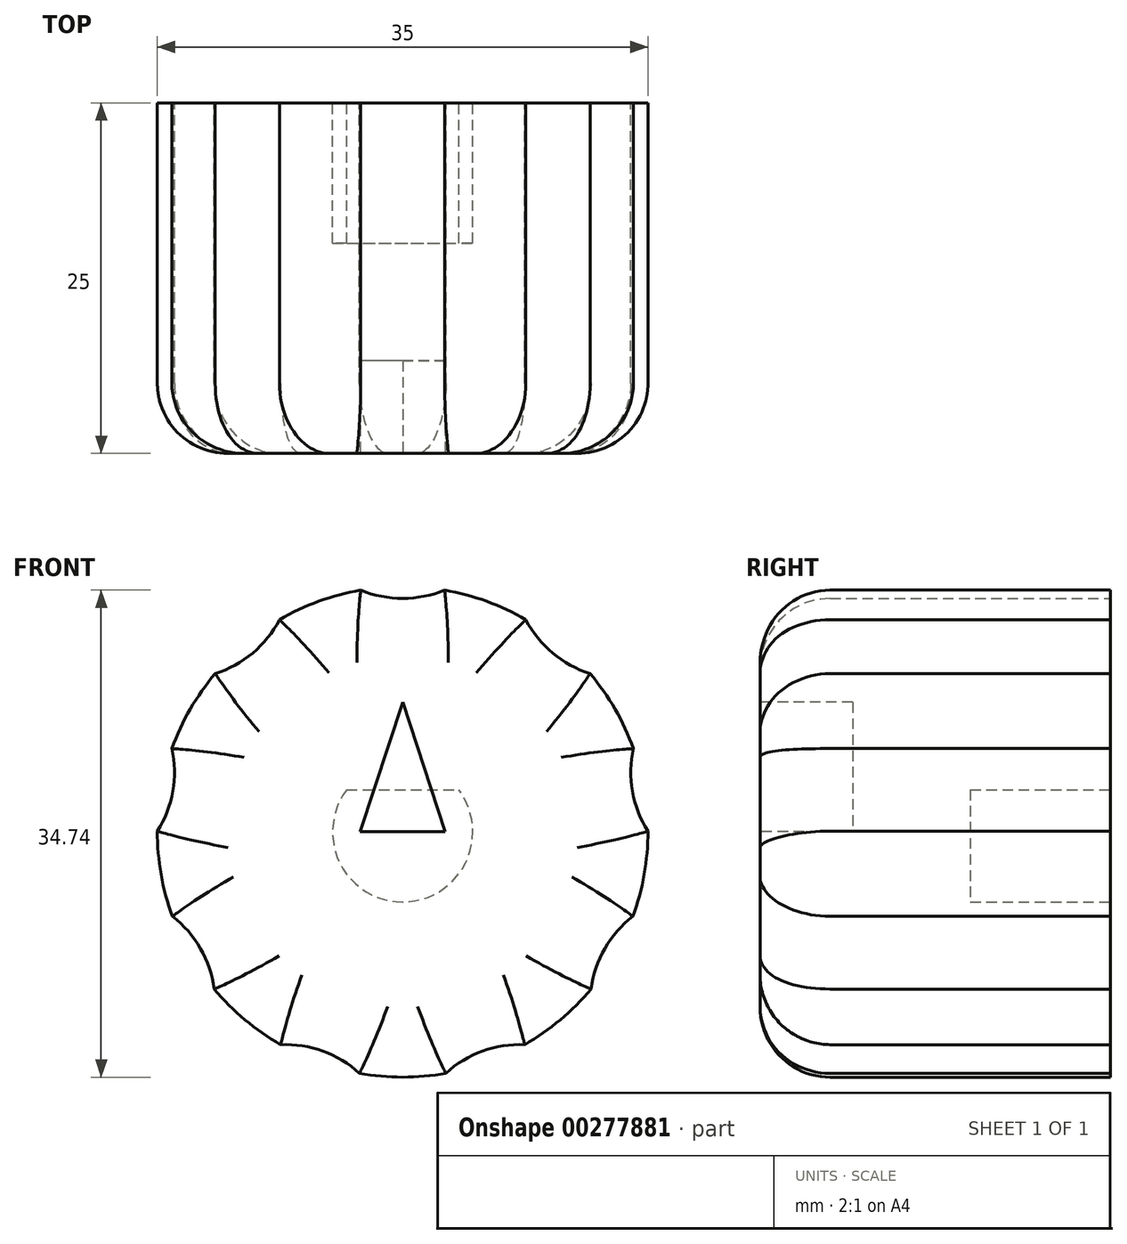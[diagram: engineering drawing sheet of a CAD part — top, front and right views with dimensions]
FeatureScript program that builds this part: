
annotation { "Feature Type Name" : "Feature", "Feature Type Description" : "" }
export const myFeature = defineFeature(function(context is Context, id is Id, definition is map)
    precondition{}
    {
        {
            var Q0;
            Q0=qCreatedBy(makeId("Front.planeOp"),FACE);
            var sketch = newSketch(context, id + "F0", { "sketchPlane" : qUnion([Q0])});
            skCircle(sketch, "E0", {"center": v(0, 0) * mm, "radius": 17.5 * mm});
            skCircle(sketch, "E1", {"center": v(0, 0) * mm, "radius": 5 * mm});
            skLineSegment(sketch, "E2", {"start": v(-4, 3) * mm, "end": v(4, 3) * mm});
            skLineSegment(sketch, "E3", {"start": v(-63, 45.04) * mm, "end": v(-24.6, 45.04) * mm, "construction": true});
            skLineSegment(sketch, "E4", {"start": v(-60.54, 31) * mm, "end": v(-26.33, 31.5) * mm, "construction": true});
            skLineSegment(sketch, "E5", {"start": v(-3, 17.24) * mm, "end": v(3, 17.24) * mm, "construction": true});
            skArc(sketch, "E6", {"start": v(-3, 17.24) * mm, "mid": v(0, 16.65) * mm, "end": v(3, 17.24) * mm});
            skArc(sketch, "E7.1.0", {"start": v(-13.37, 11.29) * mm, "mid": v(-10.7, 12.75) * mm, "end": v(-8.8, 15.13) * mm});
            skArc(sketch, "E7.2.0", {"start": v(-17.5, 0.05) * mm, "mid": v(-16.4, 2.9) * mm, "end": v(-16.46, 5.94) * mm});
            skArc(sketch, "E7.3.0", {"start": v(-13.44, -11.21) * mm, "mid": v(-14.42, -8.32) * mm, "end": v(-16.43, -6.03) * mm});
            skArc(sketch, "E7.4.0", {"start": v(-3.09, -17.23) * mm, "mid": v(-5.7, -15.64) * mm, "end": v(-8.7, -15.18) * mm});
            skArc(sketch, "E7.5.0", {"start": v(8.7, -15.18) * mm, "mid": v(5.7, -15.64) * mm, "end": v(3.09, -17.23) * mm});
            skArc(sketch, "E7.6.0", {"start": v(16.43, -6.03) * mm, "mid": v(14.42, -8.32) * mm, "end": v(13.44, -11.21) * mm});
            skArc(sketch, "E7.7.0", {"start": v(16.46, 5.94) * mm, "mid": v(16.4, 2.9) * mm, "end": v(17.5, 0.05) * mm});
            skArc(sketch, "E7.8.0", {"start": v(8.8, 15.13) * mm, "mid": v(10.7, 12.75) * mm, "end": v(13.37, 11.29) * mm});
            skSolve(sketch);
        }
        {
            var Q0;
            {var subQ13=sQuery(id+"F0.wireOp",EDGE,"E6");Q0=makeQuery(id+"F0.imprint","IMPRINT",FACE,{"disambiguationData":[TD([[makeQuery(id+"F0.imprint","IMPRINT",EDGE,{"derivedFrom":subQ13}),-1.0]])]});}
            var Q1;
            {var subQ0=sQuery(id+"F0.wireOp",EDGE,"E2");Q1=makeQuery(id+"F0.imprint","IMPRINT",FACE,{"disambiguationData":[TD([[makeQuery(id+"F0.imprint","IMPRINT",EDGE,{"derivedFrom":subQ0}),1.0]])]});}
            var Q2;
            {var subQ0=sQuery(id+"F0.wireOp",EDGE,"E2");Q2=makeQuery(id+"F0.imprint","IMPRINT",FACE,{"disambiguationData":[TD([[makeQuery(id+"F0.imprint","IMPRINT",EDGE,{"derivedFrom":subQ0}),-1.0]])]});}
            extrude(context, id + "F1", {"entities" : qUnion([Q0, Q1, Q2]), "depth" : 25 * mm});
        }
        {
            var Q0;
            {var subQ0=sQuery(id+"F0.wireOp",EDGE,"E2");Q0=makeQuery(id+"F0.imprint","IMPRINT",FACE,{"disambiguationData":[TD([[makeQuery(id+"F0.imprint","IMPRINT",EDGE,{"derivedFrom":subQ0}),-1.0]])]});}
            extrude(context, id + "F2", {"entities" : qUnion([Q0]), "operationType" : NewBodyOperationType.REMOVE, "depth" : 10 * mm});
        }
        {
            var Q0;
            Q0=makeQuery(id+"F1.opExtrude","CAP_FACE",FACE,{"disambiguationData":[OSD([sQuery(id+"F0.wireOp",EDGE,"E0"),sQuery(id+"F0.wireOp",EDGE,"E6"),sQuery(id+"F0.wireOp",EDGE,"E7.1.0"),sQuery(id+"F0.wireOp",EDGE,"E7.2.0"),sQuery(id+"F0.wireOp",EDGE,"E7.3.0"),sQuery(id+"F0.wireOp",EDGE,"E7.4.0"),sQuery(id+"F0.wireOp",EDGE,"E7.5.0"),sQuery(id+"F0.wireOp",EDGE,"E7.6.0"),sQuery(id+"F0.wireOp",EDGE,"E7.7.0"),sQuery(id+"F0.wireOp",EDGE,"E7.8.0")])],"isStart":false});
            fillet(context, id + "F3", {"entities" : qUnion([Q0]), "radius" : 5 * mm, "tangentPropagation" : true, "allowEdgeOverflow" : false});
        }
        {
            var Q0;
            Q0=makeQuery(id+"F1.opExtrude","CAP_FACE",FACE,{"disambiguationData":[OSD([sQuery(id+"F0.wireOp",EDGE,"E0"),sQuery(id+"F0.wireOp",EDGE,"E6"),sQuery(id+"F0.wireOp",EDGE,"E7.1.0"),sQuery(id+"F0.wireOp",EDGE,"E7.2.0"),sQuery(id+"F0.wireOp",EDGE,"E7.3.0"),sQuery(id+"F0.wireOp",EDGE,"E7.4.0"),sQuery(id+"F0.wireOp",EDGE,"E7.5.0"),sQuery(id+"F0.wireOp",EDGE,"E7.6.0"),sQuery(id+"F0.wireOp",EDGE,"E7.7.0"),sQuery(id+"F0.wireOp",EDGE,"E7.8.0")])],"isStart":false});
            var sketch = newSketch(context, id + "F4", { "sketchPlane" : qUnion([Q0])});
            skLineSegment(sketch, "E8", {"start": v(0, 9.24) * mm, "end": v(3.03, 0) * mm});
            skLineSegment(sketch, "E9", {"start": v(0, 0) * mm, "end": v(3.03, 0) * mm});
            skLineSegment(sketch, "E10", {"start": v(0, 9.24) * mm, "end": v(0, 0) * mm, "construction": true});
            skLineSegment(sketch, "E11.MirrorCS", {"start": v(0, 9.24) * mm, "end": v(-3.03, 0) * mm});
            skLineSegment(sketch, "E12.MirrorCS", {"start": v(0, 0) * mm, "end": v(-3.03, 0) * mm});
            skSolve(sketch);
        }
        {
            var Q0;
            Q0=makeQuery(id+"F4.imprint","IMPRINT",FACE,{"disambiguationData":[TD([[makeQuery(id+"F4.imprint","IMPRINT",EDGE,{"derivedFrom":sQuery(id+"F4.wireOp",EDGE,"E8")}),-1.0]])]});
            extrude(context, id + "F5", {"entities" : qUnion([Q0]), "operationType" : NewBodyOperationType.REMOVE, "oppositeDirection" : true, "depth" : 6.6 * mm});
        }
    });
